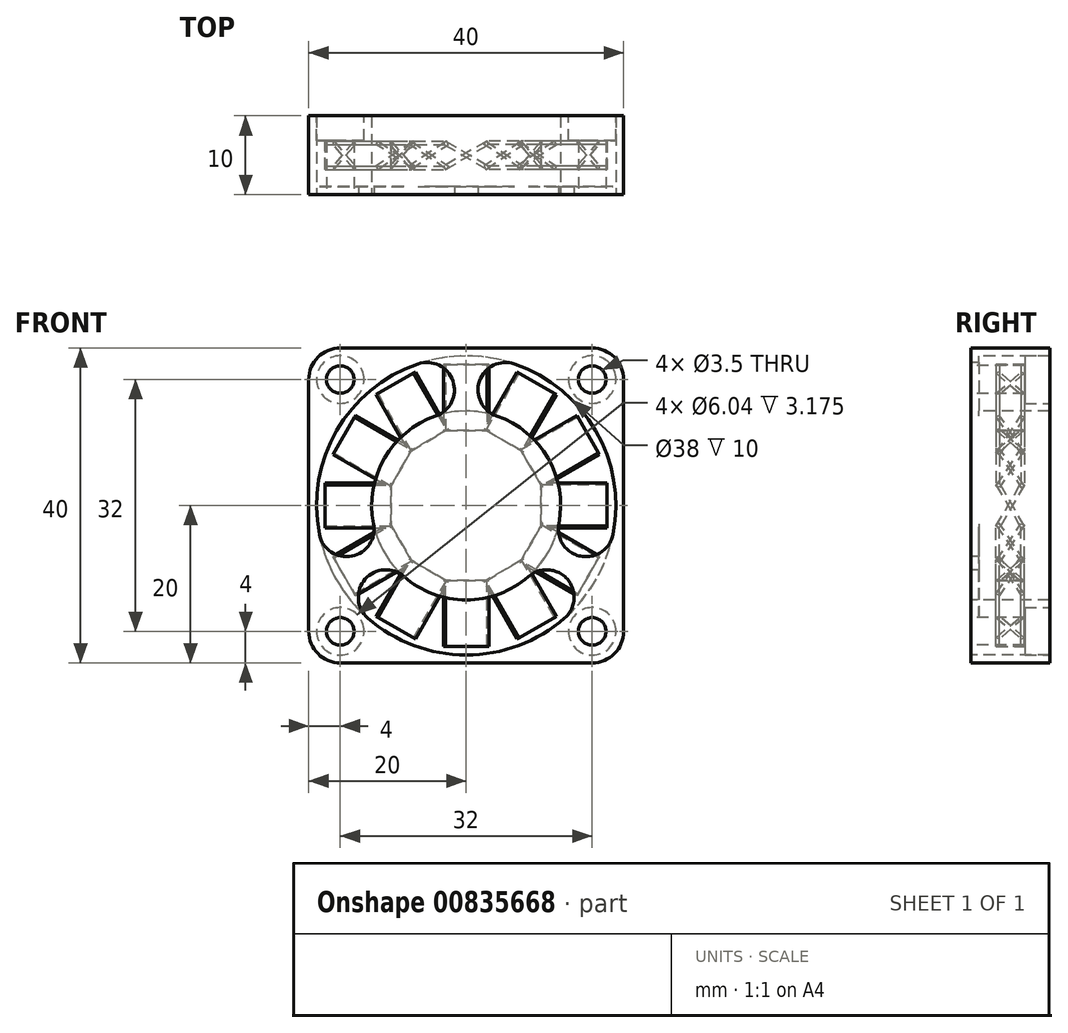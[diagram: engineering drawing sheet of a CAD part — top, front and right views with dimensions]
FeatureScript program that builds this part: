
annotation { "Feature Type Name" : "Feature", "Feature Type Description" : "" }
export const myFeature = defineFeature(function(context is Context, id is Id, definition is map)
    precondition{}
    {
        {
            var Q0;
            Q0=qCreatedBy(makeId("Front.planeOp"),FACE);
            var sketch = newSketch(context, id + "F0", { "sketchPlane" : qUnion([Q0])});
            skLineSegment(sketch, "E0.bottom", {"start": v(-20, 20) * mm, "end": v(20, 20) * mm});
            skLineSegment(sketch, "E0.top", {"start": v(-20, -20) * mm, "end": v(20, -20) * mm});
            skLineSegment(sketch, "E0.left", {"start": v(-20, 20) * mm, "end": v(-20, -20) * mm});
            skLineSegment(sketch, "E0.right", {"start": v(20, 20) * mm, "end": v(20, -20) * mm});
            skLineSegment(sketch, "E1", {"start": v(-20, -20) * mm, "end": v(20, 20) * mm, "construction": true});
            skSolve(sketch);
        }
        {
            var Q0;
            Q0=makeQuery(id+"F0.imprint","IMPRINT",FACE,{"disambiguationData":[TD([[makeQuery(id+"F0.imprint","IMPRINT",EDGE,{"derivedFrom":sQuery(id+"F0.wireOp",EDGE,"E0.bottom")}),-1.0]])]});
            extrude(context, id + "F1", {"entities" : qUnion([Q0]), "depth" : 10 * mm, "offsetDistance" : 25.4 * mm});
        }
        {
            var Q0;
            Q0=makeQuery(id+"F1.opExtrude","SWEPT_EDGE",EDGE,{"disambiguationData":[OSD([sQuery(id+"F0.wireOp",EDGE,"E0.top"),sQuery(id+"F0.wireOp",EDGE,"E0.left")])]});
            var Q1;
            Q1=makeQuery(id+"F1.opExtrude","SWEPT_EDGE",EDGE,{"disambiguationData":[OSD([sQuery(id+"F0.wireOp",EDGE,"E0.top"),sQuery(id+"F0.wireOp",EDGE,"E0.right")])]});
            var Q2;
            Q2=makeQuery(id+"F1.opExtrude","SWEPT_EDGE",EDGE,{"disambiguationData":[OSD([sQuery(id+"F0.wireOp",EDGE,"E0.bottom"),sQuery(id+"F0.wireOp",EDGE,"E0.right")])]});
            var Q3;
            Q3=makeQuery(id+"F1.opExtrude","SWEPT_EDGE",EDGE,{"disambiguationData":[OSD([sQuery(id+"F0.wireOp",EDGE,"E0.bottom"),sQuery(id+"F0.wireOp",EDGE,"E0.left")])]});
            fillet(context, id + "F2", {"entities" : qUnion([Q0, Q1, Q2, Q3]), "radius" : 4 * mm, "tangentPropagation" : true, "allowEdgeOverflow" : false});
        }
        {
            var Q0;
            Q0=makeQuery(id+"F1.opExtrude","CAP_FACE",FACE,{"disambiguationData":[OSD([sQuery(id+"F0.wireOp",EDGE,"E0.bottom"),sQuery(id+"F0.wireOp",EDGE,"E0.top"),sQuery(id+"F0.wireOp",EDGE,"E0.left"),sQuery(id+"F0.wireOp",EDGE,"E0.right")])],"isStart":true});
            shell(context, id + "F3", {"entities" : qUnion([Q0]), "thickness" : 1 * mm});
        }
        {
            var Q0;
            Q0=makeQuery(id+"F1.opExtrude","CAP_FACE",FACE,{"disambiguationData":[OSD([sQuery(id+"F0.wireOp",EDGE,"E0.bottom"),sQuery(id+"F0.wireOp",EDGE,"E0.top"),sQuery(id+"F0.wireOp",EDGE,"E0.left"),sQuery(id+"F0.wireOp",EDGE,"E0.right")])],"isStart":false});
            var sketch = newSketch(context, id + "F4", { "sketchPlane" : qUnion([Q0])});
            skArc(sketch, "E2", {"start": v(-1.5, 11.9) * mm, "mid": v(-10.4, 6) * mm, "end": v(-11.06, -4.65) * mm});
            skArc(sketch, "E3", {"start": v(-1.5, 18.94) * mm, "mid": v(-16.45, 9.5) * mm, "end": v(-17.15, -8.17) * mm});
            skLineSegment(sketch, "E4", {"start": v(-1.5, 18.94) * mm, "end": v(-1.5, 11.9) * mm});
            skLineSegment(sketch, "E5", {"start": v(1.5, 18.94) * mm, "end": v(1.5, 11.9) * mm});
            skLineSegment(sketch, "E6.1.0", {"start": v(-15.65, -10.77) * mm, "end": v(-9.56, -7.25) * mm});
            skLineSegment(sketch, "E6.1.1", {"start": v(-17.15, -8.17) * mm, "end": v(-11.06, -4.65) * mm});
            skLineSegment(sketch, "E6.2.0", {"start": v(17.15, -8.17) * mm, "end": v(11.06, -4.65) * mm});
            skLineSegment(sketch, "E6.2.1", {"start": v(15.65, -10.77) * mm, "end": v(9.56, -7.25) * mm});
            skArc(sketch, "E7.trimOffspring", {"start": v(-9.56, -7.25) * mm, "mid": v(0, -12) * mm, "end": v(9.56, -7.25) * mm});
            skArc(sketch, "E8.trimOffspring", {"start": v(-15.65, -10.77) * mm, "mid": v(0, -19) * mm, "end": v(15.65, -10.77) * mm});
            skArc(sketch, "E9.trimOffspring", {"start": v(11.06, -4.65) * mm, "mid": v(10.4, 6) * mm, "end": v(1.5, 11.9) * mm});
            skArc(sketch, "E10.trimOffspring", {"start": v(17.15, -8.17) * mm, "mid": v(16.45, 9.5) * mm, "end": v(1.5, 18.94) * mm});
            skSolve(sketch);
        }
        {
            var Q0;
            Q0 = qSketchRegion(id + "F4", true);
            extrude(context, id + "F5", {"entities" : qUnion([Q0]), "operationType" : NewBodyOperationType.REMOVE, "endBound" : BoundingType.THROUGH_ALL, "oppositeDirection" : true, "depth" : 25.4 * mm, "offsetDistance" : 25.4 * mm});
        }
        {
            var Q0;
            Q0=makeQuery(id+"F1.opExtrude","CAP_FACE",FACE,{"disambiguationData":[OSD([sQuery(id+"F0.wireOp",EDGE,"E0.bottom"),sQuery(id+"F0.wireOp",EDGE,"E0.top"),sQuery(id+"F0.wireOp",EDGE,"E0.left"),sQuery(id+"F0.wireOp",EDGE,"E0.right")])],"isStart":false});
            var sketch = newSketch(context, id + "F6", { "sketchPlane" : qUnion([Q0])});
            skArc(sketch, "E11", {"start": v(6.13, 17.98) * mm, "mid": v(1.69, 15.8) * mm, "end": v(3.87, 11.36) * mm});
            skArc(sketch, "E12", {"start": v(11.77, -2.33) * mm, "mid": v(14.53, -6.44) * mm, "end": v(18.64, -3.68) * mm});
            skLineSegment(sketch, "E13.0", {"start": v(1.5, 18.94) * mm, "end": v(1.5, 11.9) * mm});
            skLineSegment(sketch, "E14.0", {"start": v(17.15, -8.17) * mm, "end": v(11.06, -4.65) * mm});
            skArc(sketch, "E15", {"start": v(6.13, 17.98) * mm, "mid": v(3.84, 18.6) * mm, "end": v(1.5, 18.94) * mm});
            skArc(sketch, "E16", {"start": v(1.5, 11.9) * mm, "mid": v(2.67, 11.57) * mm, "end": v(3.87, 11.36) * mm});
            skArc(sketch, "E17", {"start": v(11.77, -2.33) * mm, "mid": v(11.36, -3.47) * mm, "end": v(11.06, -4.65) * mm});
            skArc(sketch, "E18", {"start": v(17.15, -8.17) * mm, "mid": v(18.04, -5.97) * mm, "end": v(18.64, -3.68) * mm});
            skArc(sketch, "E19.1.0", {"start": v(-1.5, 18.94) * mm, "mid": v(-3.84, 18.6) * mm, "end": v(-6.13, 17.98) * mm});
            skLineSegment(sketch, "E19.1.1", {"start": v(-17.15, -8.17) * mm, "end": v(-11.06, -4.65) * mm});
            skLineSegment(sketch, "E19.1.2", {"start": v(-1.5, 18.94) * mm, "end": v(-1.5, 11.9) * mm});
            skArc(sketch, "E19.1.3", {"start": v(-3.87, 11.36) * mm, "mid": v(-1.69, 15.8) * mm, "end": v(-6.13, 17.98) * mm});
            skArc(sketch, "E19.1.4", {"start": v(-18.64, -3.68) * mm, "mid": v(-14.53, -6.44) * mm, "end": v(-11.77, -2.33) * mm});
            skArc(sketch, "E19.1.5", {"start": v(-18.64, -3.68) * mm, "mid": v(-18.04, -5.97) * mm, "end": v(-17.15, -8.17) * mm});
            skArc(sketch, "E19.1.6", {"start": v(-3.87, 11.36) * mm, "mid": v(-2.67, 11.57) * mm, "end": v(-1.5, 11.9) * mm});
            skArc(sketch, "E19.1.7", {"start": v(-11.06, -4.65) * mm, "mid": v(-11.36, -3.47) * mm, "end": v(-11.77, -2.33) * mm});
            skArc(sketch, "E19.2.0", {"start": v(-15.65, -10.77) * mm, "mid": v(-14.2, -12.63) * mm, "end": v(-12.51, -14.3) * mm});
            skLineSegment(sketch, "E19.2.1", {"start": v(15.65, -10.77) * mm, "end": v(9.56, -7.25) * mm});
            skLineSegment(sketch, "E19.2.2", {"start": v(-15.65, -10.77) * mm, "end": v(-9.56, -7.25) * mm});
            skArc(sketch, "E19.2.3", {"start": v(-7.9, -9.03) * mm, "mid": v(-12.84, -9.36) * mm, "end": v(-12.51, -14.3) * mm});
            skArc(sketch, "E19.2.4", {"start": v(12.51, -14.3) * mm, "mid": v(12.84, -9.36) * mm, "end": v(7.9, -9.03) * mm});
            skArc(sketch, "E19.2.5", {"start": v(12.51, -14.3) * mm, "mid": v(14.2, -12.63) * mm, "end": v(15.65, -10.77) * mm});
            skArc(sketch, "E19.2.6", {"start": v(-7.9, -9.03) * mm, "mid": v(-8.69, -8.1) * mm, "end": v(-9.56, -7.25) * mm});
            skArc(sketch, "E19.2.7", {"start": v(9.56, -7.25) * mm, "mid": v(8.69, -8.1) * mm, "end": v(7.9, -9.03) * mm});
            skSolve(sketch);
        }
        {
            var Q0;
            Q0 = qSketchRegion(id + "F6", true);
            var Q1;
            Q1=makeQuery(id+"F3.opShell","OFFSET_FACE",FACE,{"disambiguationData":[OSD([sQuery(id+"F0.wireOp",EDGE,"E0.bottom"),sQuery(id+"F0.wireOp",EDGE,"E0.top"),sQuery(id+"F0.wireOp",EDGE,"E0.left"),sQuery(id+"F0.wireOp",EDGE,"E0.right")])]});
            extrude(context, id + "F7", {"entities" : qUnion([Q0]), "operationType" : NewBodyOperationType.ADD, "oppositeDirection" : true, "depth" : 1 * mm, "endBoundEntityFace" : qUnion([Q1]), "offsetDistance" : 25.4 * mm});
        }
        {
            var Q0;
            {var subQ0=sQuery(id+"F6.wireOp",EDGE,"E19.2.3");var subQ1=sQuery(id+"F6.wireOp",EDGE,"E19.2.2");var subQ2=sQuery(id+"F6.wireOp",EDGE,"E19.2.4");var subQ3=sQuery(id+"F6.wireOp",EDGE,"E19.2.1");var subQ4=sQuery(id+"F6.wireOp",EDGE,"E19.1.3");var subQ5=sQuery(id+"F6.wireOp",EDGE,"E19.1.2");var subQ6=sQuery(id+"F6.wireOp",EDGE,"E19.1.4");var subQ7=sQuery(id+"F6.wireOp",EDGE,"E19.1.1");var subQ8=sQuery(id+"F6.wireOp",EDGE,"E14.0");var subQ9=sQuery(id+"F6.wireOp",EDGE,"E12");var subQ10=sQuery(id+"F6.wireOp",EDGE,"E13.0");var subQ11=sQuery(id+"F6.wireOp",EDGE,"E11");Q0=makeQuery(id+"F7.boolean.opBoolean","MERGE",FACE,{"derivedFrom":[makeQuery(id+"F3.opShell","OFFSET_FACE",FACE,{"disambiguationData":[OSD([sQuery(id+"F0.wireOp",EDGE,"E0.bottom"),sQuery(id+"F0.wireOp",EDGE,"E0.top"),sQuery(id+"F0.wireOp",EDGE,"E0.left"),sQuery(id+"F0.wireOp",EDGE,"E0.right")])]}),makeQuery(id+"F7.opExtrude","CAP_FACE",FACE,{"disambiguationData":[OSD([subQ11,subQ10,sQuery(id+"F6.wireOp",EDGE,"E15")])],"isStart":false}),makeQuery(id+"F7.opExtrude","CAP_FACE",FACE,{"disambiguationData":[OSD([subQ11,subQ10,sQuery(id+"F6.wireOp",EDGE,"E16")])],"isStart":false}),makeQuery(id+"F7.opExtrude","CAP_FACE",FACE,{"disambiguationData":[OSD([subQ9,subQ8,sQuery(id+"F6.wireOp",EDGE,"E17")])],"isStart":false}),makeQuery(id+"F7.opExtrude","CAP_FACE",FACE,{"disambiguationData":[OSD([subQ9,subQ8,sQuery(id+"F6.wireOp",EDGE,"E18")])],"isStart":false}),makeQuery(id+"F7.opExtrude","CAP_FACE",FACE,{"disambiguationData":[OSD([sQuery(id+"F6.wireOp",EDGE,"E19.1.0"),subQ5,subQ4])],"isStart":false}),makeQuery(id+"F7.opExtrude","CAP_FACE",FACE,{"disambiguationData":[OSD([subQ7,subQ6,sQuery(id+"F6.wireOp",EDGE,"E19.1.5")])],"isStart":false}),makeQuery(id+"F7.opExtrude","CAP_FACE",FACE,{"disambiguationData":[OSD([subQ7,subQ6,sQuery(id+"F6.wireOp",EDGE,"E19.1.7")])],"isStart":false}),makeQuery(id+"F7.opExtrude","CAP_FACE",FACE,{"disambiguationData":[OSD([subQ5,subQ4,sQuery(id+"F6.wireOp",EDGE,"E19.1.6")])],"isStart":false}),makeQuery(id+"F7.opExtrude","CAP_FACE",FACE,{"disambiguationData":[OSD([sQuery(id+"F6.wireOp",EDGE,"E19.2.0"),subQ1,subQ0])],"isStart":false}),makeQuery(id+"F7.opExtrude","CAP_FACE",FACE,{"disambiguationData":[OSD([subQ3,subQ2,sQuery(id+"F6.wireOp",EDGE,"E19.2.5")])],"isStart":false}),makeQuery(id+"F7.opExtrude","CAP_FACE",FACE,{"disambiguationData":[OSD([subQ3,subQ2,sQuery(id+"F6.wireOp",EDGE,"E19.2.7")])],"isStart":false}),makeQuery(id+"F7.opExtrude","CAP_FACE",FACE,{"disambiguationData":[OSD([subQ1,subQ0,sQuery(id+"F6.wireOp",EDGE,"E19.2.6")])],"isStart":false})]});}
            var sketch = newSketch(context, id + "F8", { "sketchPlane" : qUnion([Q0])});
            skCircle(sketch, "E20", {"center": v(0, 0) * mm, "radius": 12 * mm});
            skSolve(sketch);
        }
        {
            var Q0;
            {var subQ0=sQuery(id+"F8.wireOp",EDGE,"E20");var subQ1=sQuery(id+"F6.wireOp",EDGE,"E19.1.3");var subQ3=makeQuery(id+"F6.imprint","INTERSECT",VERTEX,{"derivedFrom":[sQuery(id+"F6.wireOp",EDGE,"E19.1.2"),subQ1]});var subQ5=makeQuery(id+"F8.imprint","INTERSECT",VERTEX,{"derivedFrom":[makeQuery(id+"F7.boolean.opBoolean","MERGE",EDGE,{"derivedFrom":[makeQuery(id+"F7.opExtrude","CAP_EDGE",EDGE,{"disambiguationData":[OSD([subQ1]),TDD([makeQuery(id+"F6.imprint","IMPRINT",EDGE,{"disambiguationData":[TD([[subQ3,1.0]])],"derivedFrom":subQ1})])],"isStart":false}),makeQuery(id+"F7.opExtrude","CAP_EDGE",EDGE,{"disambiguationData":[OSD([subQ1]),TDD([makeQuery(id+"F6.imprint","IMPRINT",EDGE,{"disambiguationData":[TD([[subQ3,-1.0]])],"derivedFrom":subQ1})])],"isStart":false})]}),subQ0]});var subQ19=sQuery(id+"F6.wireOp",EDGE,"E11");var subQ20=makeQuery(id+"F6.imprint","INTERSECT",VERTEX,{"derivedFrom":[subQ19,sQuery(id+"F6.wireOp",EDGE,"E13.0")]});var subQ21=makeQuery(id+"F8.imprint","INTERSECT",VERTEX,{"derivedFrom":[makeQuery(id+"F7.boolean.opBoolean","MERGE",EDGE,{"derivedFrom":[makeQuery(id+"F7.opExtrude","CAP_EDGE",EDGE,{"disambiguationData":[OSD([subQ19]),TDD([makeQuery(id+"F6.imprint","IMPRINT",EDGE,{"disambiguationData":[TD([[subQ20,1.0]])],"derivedFrom":subQ19})])],"isStart":false}),makeQuery(id+"F7.opExtrude","CAP_EDGE",EDGE,{"disambiguationData":[OSD([subQ19]),TDD([makeQuery(id+"F6.imprint","IMPRINT",EDGE,{"disambiguationData":[TD([[subQ20,-1.0]])],"derivedFrom":subQ19})])],"isStart":false})]}),subQ0]});Q0=makeQuery(id+"F8.imprint","IMPRINT",FACE,{"disambiguationData":[TD([[makeQuery(id+"F8.imprint","IMPRINT",EDGE,{"disambiguationData":[TD([[subQ21,1.0],[subQ5,-1.0]])],"derivedFrom":subQ0}),1.0]])]});}
            var Q1;
            Q1=makeQuery(id+"F1.opExtrude","CAP_FACE",FACE,{"disambiguationData":[OSD([sQuery(id+"F0.wireOp",EDGE,"E0.bottom"),sQuery(id+"F0.wireOp",EDGE,"E0.top"),sQuery(id+"F0.wireOp",EDGE,"E0.left"),sQuery(id+"F0.wireOp",EDGE,"E0.right")])],"isStart":true});
            extrude(context, id + "F9", {"entities" : qUnion([Q0]), "operationType" : NewBodyOperationType.ADD, "endBound" : BoundingType.UP_TO_SURFACE, "depth" : 25.4 * mm, "endBoundEntityFace" : qUnion([Q1]), "offsetDistance" : 25.4 * mm});
        }
        {
            var Q0;
            Q0=qCreatedBy(makeId("Top.planeOp"),FACE);
            cPlane(context, id + "F10", {"entities" : qUnion([Q0]), "cplaneType" : CPlaneType.OFFSET, "offset" : 9.52 * mm, "width" : 152.4 * mm, "height" : 152.4 * mm});
        }
        {
            var Q0;
            Q0=qCreatedBy(id+"F10.planeOp",FACE);
            var sketch = newSketch(context, id + "F11", { "sketchPlane" : qUnion([Q0])});
            skLineSegment(sketch, "E21", {"start": v(-2.75, -3.41) * mm, "end": v(2.75, -6.59) * mm, "construction": true});
            skLineSegment(sketch, "E22", {"start": v(-16, -5) * mm, "end": v(0, -5) * mm, "construction": true});
            skLineSegment(sketch, "E23", {"start": v(-2.87, -3.63) * mm, "end": v(-2.62, -3.2) * mm});
            skLineSegment(sketch, "E24", {"start": v(-2.62, -3.2) * mm, "end": v(2.87, -6.37) * mm});
            skLineSegment(sketch, "E25", {"start": v(2.87, -6.37) * mm, "end": v(2.62, -6.8) * mm});
            skLineSegment(sketch, "E26", {"start": v(2.62, -6.8) * mm, "end": v(-2.87, -3.63) * mm});
            skSolve(sketch);
        }
        {
            var Q0;
            Q0 = qSketchRegion(id + "F11", true);
            extrude(context, id + "F12", {"entities" : qUnion([Q0]), "depth" : 8.38 * mm, "offsetDistance" : 25.4 * mm});
        }
        {
            var Q0;
            Q0=makeQuery(id+"F12.opExtrude","SWEPT_BODY",BODY,{"disambiguationData":[OSD([sQuery(id+"F11.wireOp",EDGE,"E23"),sQuery(id+"F11.wireOp",EDGE,"E24"),sQuery(id+"F11.wireOp",EDGE,"E25"),sQuery(id+"F11.wireOp",EDGE,"E26")])]});
            var Q1;
            Q1=makeQuery(id+"F9.boolean.opBoolean","MERGE",FACE,{"derivedFrom":[makeQuery(id+"F5.boolean.opBoolean","COPY",FACE,{"derivedFrom":makeQuery(id+"F5.opExtrude","SWEPT_FACE",FACE,{"disambiguationData":[OSD([sQuery(id+"F4.wireOp",EDGE,"E2")])]})}),makeQuery(id+"F5.boolean.opBoolean","COPY",FACE,{"derivedFrom":makeQuery(id+"F5.opExtrude","SWEPT_FACE",FACE,{"disambiguationData":[OSD([sQuery(id+"F4.wireOp",EDGE,"E7.trimOffspring")])]})}),makeQuery(id+"F5.boolean.opBoolean","COPY",FACE,{"derivedFrom":makeQuery(id+"F5.opExtrude","SWEPT_FACE",FACE,{"disambiguationData":[OSD([sQuery(id+"F4.wireOp",EDGE,"E9.trimOffspring")])]})}),makeQuery(id+"F9.opExtrude","SWEPT_FACE",FACE,{"disambiguationData":[OSD([sQuery(id+"F8.wireOp",EDGE,"E20")])]})]});
            circularPattern(context, id + "F13", {"entities" : qUnion([Q0]), "axis" : qUnion([Q1]), "angle" : 360 * degree, "instanceCount" : 12, "equalSpace" : true});
        }
        {
            var Q0;
            {var subQ0=sQuery(id+"F6.wireOp",EDGE,"E19.1.6");var subQ1=sQuery(id+"F6.wireOp",EDGE,"E19.1.3");var subQ2=sQuery(id+"F6.wireOp",EDGE,"E19.1.2");var subQ3=makeQuery(id+"F7.opExtrude","CAP_FACE",FACE,{"disambiguationData":[OSD([subQ2,subQ1,subQ0])],"isStart":false});var subQ4=sQuery(id+"F6.wireOp",EDGE,"E19.1.0");var subQ5=makeQuery(id+"F7.opExtrude","CAP_FACE",FACE,{"disambiguationData":[OSD([subQ4,subQ2,subQ1])],"isStart":false});var subQ6=sQuery(id+"F6.wireOp",EDGE,"E14.0");var subQ7=sQuery(id+"F6.wireOp",EDGE,"E12");var subQ8=makeQuery(id+"F7.opExtrude","CAP_FACE",FACE,{"disambiguationData":[OSD([subQ7,subQ6,sQuery(id+"F6.wireOp",EDGE,"E17")])],"isStart":false});var subQ9=sQuery(id+"F6.wireOp",EDGE,"E19.1.4");var subQ10=sQuery(id+"F6.wireOp",EDGE,"E19.1.1");var subQ11=makeQuery(id+"F7.opExtrude","CAP_FACE",FACE,{"disambiguationData":[OSD([subQ10,subQ9,sQuery(id+"F6.wireOp",EDGE,"E19.1.7")])],"isStart":false});var subQ12=sQuery(id+"F6.wireOp",EDGE,"E16");var subQ13=sQuery(id+"F6.wireOp",EDGE,"E13.0");var subQ14=sQuery(id+"F6.wireOp",EDGE,"E11");var subQ15=makeQuery(id+"F7.opExtrude","CAP_FACE",FACE,{"disambiguationData":[OSD([subQ14,subQ13,subQ12])],"isStart":false});var subQ16=sQuery(id+"F6.wireOp",EDGE,"E19.2.3");var subQ17=sQuery(id+"F6.wireOp",EDGE,"E19.2.2");var subQ18=makeQuery(id+"F7.opExtrude","CAP_FACE",FACE,{"disambiguationData":[OSD([subQ17,subQ16,sQuery(id+"F6.wireOp",EDGE,"E19.2.6")])],"isStart":false});var subQ21=makeQuery(id+"F7.opExtrude","CAP_FACE",FACE,{"disambiguationData":[OSD([subQ10,subQ9,sQuery(id+"F6.wireOp",EDGE,"E19.1.5")])],"isStart":false});var subQ22=sQuery(id+"F6.wireOp",EDGE,"E15");var subQ23=makeQuery(id+"F7.opExtrude","CAP_FACE",FACE,{"disambiguationData":[OSD([subQ14,subQ13,subQ22])],"isStart":false});var subQ27=sQuery(id+"F0.wireOp",EDGE,"E0.bottom");var subQ28=sQuery(id+"F0.wireOp",EDGE,"E0.right");var subQ29=makeQuery(id+"F7.opExtrude","CAP_FACE",FACE,{"disambiguationData":[OSD([subQ7,subQ6,sQuery(id+"F6.wireOp",EDGE,"E18")])],"isStart":false});var subQ30=sQuery(id+"F0.wireOp",EDGE,"E0.left");var subQ31=makeQuery(id+"F3.opShell","OFFSET_FACE",FACE,{"disambiguationData":[OSD([subQ27,sQuery(id+"F0.wireOp",EDGE,"E0.top"),subQ30,subQ28])]});var subQ33=makeQuery(id+"F7.opExtrude","CAP_FACE",FACE,{"disambiguationData":[OSD([sQuery(id+"F6.wireOp",EDGE,"E19.2.0"),subQ17,subQ16])],"isStart":false});var subQ34=sQuery(id+"F6.wireOp",EDGE,"E19.2.4");var subQ35=sQuery(id+"F6.wireOp",EDGE,"E19.2.1");var subQ36=makeQuery(id+"F7.opExtrude","CAP_FACE",FACE,{"disambiguationData":[OSD([subQ35,subQ34,sQuery(id+"F6.wireOp",EDGE,"E19.2.5")])],"isStart":false});var subQ37=makeQuery(id+"F7.opExtrude","CAP_FACE",FACE,{"disambiguationData":[OSD([subQ35,subQ34,sQuery(id+"F6.wireOp",EDGE,"E19.2.7")])],"isStart":false});Q0=makeQuery(id+"F9.boolean.opBoolean","SPLIT",FACE,{"disambiguationData":[TD([makeQuery(id+"F3.opShell","OFFSET_FACE",FACE,{"disambiguationData":[OSD([subQ27])]})])],"derivedFrom":makeQuery(id+"F7.boolean.opBoolean","MERGE",FACE,{"derivedFrom":[subQ31,subQ23,subQ15,subQ8,subQ29,subQ5,subQ21,subQ11,subQ3,subQ33,subQ36,subQ37,subQ18]})});}
            var sketch = newSketch(context, id + "F14", { "sketchPlane" : qUnion([Q0])});
            skLineSegment(sketch, "E27.0", {"start": v(16, 19) * mm, "end": v(-16, 19) * mm});
            skArc(sketch, "E27.1", {"start": v(-16, 19) * mm, "mid": v(-18.12, 18.12) * mm, "end": v(-19, 16) * mm});
            skLineSegment(sketch, "E27.2", {"start": v(-19, 16) * mm, "end": v(-19, -16) * mm});
            skLineSegment(sketch, "E27.3", {"start": v(19, 16) * mm, "end": v(19, -16) * mm});
            skArc(sketch, "E27.4", {"start": v(19, 16) * mm, "mid": v(18.12, 18.12) * mm, "end": v(16, 19) * mm});
            skArc(sketch, "E27.5", {"start": v(-19, -16) * mm, "mid": v(-18.12, -18.12) * mm, "end": v(-16, -19) * mm});
            skLineSegment(sketch, "E27.6", {"start": v(16, -19) * mm, "end": v(-16, -19) * mm});
            skArc(sketch, "E27.7", {"start": v(16, -19) * mm, "mid": v(18.12, -18.12) * mm, "end": v(19, -16) * mm});
            skCircle(sketch, "E28", {"center": v(0, 0) * mm, "radius": 19 * mm});
            skSolve(sketch);
        }
        {
            var Q0;
            {var subQ6=sQuery(id+"F14.wireOp",EDGE,"E27.1");Q0=makeQuery(id+"F14.imprint","IMPRINT",FACE,{"disambiguationData":[TD([[makeQuery(id+"F14.imprint","IMPRINT",EDGE,{"derivedFrom":subQ6}),-1.0]])]});}
            var Q1;
            {var subQ6=sQuery(id+"F14.wireOp",EDGE,"E27.4");Q1=makeQuery(id+"F14.imprint","IMPRINT",FACE,{"disambiguationData":[TD([[makeQuery(id+"F14.imprint","IMPRINT",EDGE,{"derivedFrom":subQ6}),-1.0]])]});}
            var Q2;
            {var subQ3=sQuery(id+"F14.wireOp",EDGE,"E27.7");Q2=makeQuery(id+"F14.imprint","IMPRINT",FACE,{"disambiguationData":[TD([[makeQuery(id+"F14.imprint","IMPRINT",EDGE,{"derivedFrom":subQ3}),1.0]])]});}
            var Q3;
            {var subQ3=sQuery(id+"F14.wireOp",EDGE,"E27.5");Q3=makeQuery(id+"F14.imprint","IMPRINT",FACE,{"disambiguationData":[TD([[makeQuery(id+"F14.imprint","IMPRINT",EDGE,{"derivedFrom":subQ3}),1.0]])]});}
            var Q4;
            Q4=makeQuery(id+"F1.opExtrude","CAP_FACE",FACE,{"disambiguationData":[OSD([sQuery(id+"F0.wireOp",EDGE,"E0.bottom"),sQuery(id+"F0.wireOp",EDGE,"E0.top"),sQuery(id+"F0.wireOp",EDGE,"E0.left"),sQuery(id+"F0.wireOp",EDGE,"E0.right")])],"isStart":true});
            extrude(context, id + "F15", {"entities" : qUnion([Q0, Q1, Q2, Q3]), "operationType" : NewBodyOperationType.ADD, "endBound" : BoundingType.UP_TO_SURFACE, "depth" : 25.4 * mm, "endBoundEntityFace" : qUnion([Q4]), "offsetDistance" : 25.4 * mm});
        }
        {
            var Q0;
            {var subQ0=sQuery(id+"F6.wireOp",EDGE,"E19.2.3");var subQ1=sQuery(id+"F6.wireOp",EDGE,"E19.2.2");var subQ2=sQuery(id+"F6.wireOp",EDGE,"E19.2.4");var subQ3=sQuery(id+"F6.wireOp",EDGE,"E19.2.1");var subQ4=sQuery(id+"F6.wireOp",EDGE,"E19.1.3");var subQ5=sQuery(id+"F6.wireOp",EDGE,"E19.1.2");var subQ6=sQuery(id+"F6.wireOp",EDGE,"E19.1.4");var subQ7=sQuery(id+"F6.wireOp",EDGE,"E19.1.1");var subQ8=sQuery(id+"F6.wireOp",EDGE,"E14.0");var subQ9=sQuery(id+"F6.wireOp",EDGE,"E12");var subQ10=sQuery(id+"F6.wireOp",EDGE,"E13.0");var subQ11=sQuery(id+"F6.wireOp",EDGE,"E11");Q0=makeQuery(id+"F7.boolean.opBoolean","MERGE",FACE,{"derivedFrom":[makeQuery(id+"F1.opExtrude","CAP_FACE",FACE,{"disambiguationData":[OSD([sQuery(id+"F0.wireOp",EDGE,"E0.bottom"),sQuery(id+"F0.wireOp",EDGE,"E0.top"),sQuery(id+"F0.wireOp",EDGE,"E0.left"),sQuery(id+"F0.wireOp",EDGE,"E0.right")])],"isStart":false}),makeQuery(id+"F7.opExtrude","CAP_FACE",FACE,{"disambiguationData":[OSD([subQ11,subQ10,sQuery(id+"F6.wireOp",EDGE,"E15")])],"isStart":true}),makeQuery(id+"F7.opExtrude","CAP_FACE",FACE,{"disambiguationData":[OSD([subQ11,subQ10,sQuery(id+"F6.wireOp",EDGE,"E16")])],"isStart":true}),makeQuery(id+"F7.opExtrude","CAP_FACE",FACE,{"disambiguationData":[OSD([subQ9,subQ8,sQuery(id+"F6.wireOp",EDGE,"E17")])],"isStart":true}),makeQuery(id+"F7.opExtrude","CAP_FACE",FACE,{"disambiguationData":[OSD([subQ9,subQ8,sQuery(id+"F6.wireOp",EDGE,"E18")])],"isStart":true}),makeQuery(id+"F7.opExtrude","CAP_FACE",FACE,{"disambiguationData":[OSD([sQuery(id+"F6.wireOp",EDGE,"E19.1.0"),subQ5,subQ4])],"isStart":true}),makeQuery(id+"F7.opExtrude","CAP_FACE",FACE,{"disambiguationData":[OSD([subQ7,subQ6,sQuery(id+"F6.wireOp",EDGE,"E19.1.5")])],"isStart":true}),makeQuery(id+"F7.opExtrude","CAP_FACE",FACE,{"disambiguationData":[OSD([subQ7,subQ6,sQuery(id+"F6.wireOp",EDGE,"E19.1.7")])],"isStart":true}),makeQuery(id+"F7.opExtrude","CAP_FACE",FACE,{"disambiguationData":[OSD([subQ5,subQ4,sQuery(id+"F6.wireOp",EDGE,"E19.1.6")])],"isStart":true}),makeQuery(id+"F7.opExtrude","CAP_FACE",FACE,{"disambiguationData":[OSD([sQuery(id+"F6.wireOp",EDGE,"E19.2.0"),subQ1,subQ0])],"isStart":true}),makeQuery(id+"F7.opExtrude","CAP_FACE",FACE,{"disambiguationData":[OSD([subQ3,subQ2,sQuery(id+"F6.wireOp",EDGE,"E19.2.5")])],"isStart":true}),makeQuery(id+"F7.opExtrude","CAP_FACE",FACE,{"disambiguationData":[OSD([subQ3,subQ2,sQuery(id+"F6.wireOp",EDGE,"E19.2.7")])],"isStart":true}),makeQuery(id+"F7.opExtrude","CAP_FACE",FACE,{"disambiguationData":[OSD([subQ1,subQ0,sQuery(id+"F6.wireOp",EDGE,"E19.2.6")])],"isStart":true})]});}
            var sketch = newSketch(context, id + "F16", { "sketchPlane" : qUnion([Q0])});
            skLineSegment(sketch, "E29.bottom", {"start": v(-16, 16) * mm, "end": v(16, 16) * mm, "construction": true});
            skLineSegment(sketch, "E29.top", {"start": v(-16, -16) * mm, "end": v(16, -16) * mm, "construction": true});
            skLineSegment(sketch, "E29.left", {"start": v(-16, 16) * mm, "end": v(-16, -16) * mm, "construction": true});
            skLineSegment(sketch, "E29.right", {"start": v(16, 16) * mm, "end": v(16, -16) * mm, "construction": true});
            skLineSegment(sketch, "E30", {"start": v(-16, -16) * mm, "end": v(16, 16) * mm, "construction": true});
            skSolve(sketch);
        }
        {
            var Q0;
            Q0=sQuery(id+"F16.wireOp",VERTEX,"E29.bottom.start");
            var Q1;
            Q1=sQuery(id+"F16.wireOp",VERTEX,"E29.bottom.end");
            var Q2;
            Q2=sQuery(id+"F16.wireOp",VERTEX,"E29.top.start");
            var Q3;
            Q3=sQuery(id+"F16.wireOp",VERTEX,"E29.top.end");
            var Q4;
            Q4=makeQuery(id+"F1.opExtrude","SWEPT_BODY",BODY,{"disambiguationData":[OSD([sQuery(id+"F0.wireOp",EDGE,"E0.bottom"),sQuery(id+"F0.wireOp",EDGE,"E0.top"),sQuery(id+"F0.wireOp",EDGE,"E0.left"),sQuery(id+"F0.wireOp",EDGE,"E0.right")])]});
            hole(context, id + "F17", {"style" : HoleStyle.SIMPLE, "endStyle" : HoleEndStyle.THROUGH, "holeDiameter" : 3.5 * mm, "majorDiameter" : 6.35 * mm, "isTappedThrough" : true, "tappedDepth" : 12.7 * mm, "tapClearance" : 3, "startFromSketch" : true, "locations" : qUnion([Q0, Q1, Q2, Q3]), "scope" : qUnion([Q4])});
        }
        {
            var Q0;
            {var subQ0=sQuery(id+"F14.wireOp",EDGE,"E28");var subQ1=sQuery(id+"F14.wireOp",EDGE,"E27.6");var subQ2=sQuery(id+"F14.wireOp",EDGE,"E27.3");var subQ3=sQuery(id+"F14.wireOp",EDGE,"E27.2");var subQ4=sQuery(id+"F14.wireOp",EDGE,"E27.0");Q0=makeQuery(id+"F15.boolean.opBoolean","MERGE",FACE,{"derivedFrom":[makeQuery(id+"F1.opExtrude","CAP_FACE",FACE,{"disambiguationData":[OSD([sQuery(id+"F0.wireOp",EDGE,"E0.bottom"),sQuery(id+"F0.wireOp",EDGE,"E0.top"),sQuery(id+"F0.wireOp",EDGE,"E0.left"),sQuery(id+"F0.wireOp",EDGE,"E0.right")])],"isStart":true}),makeQuery(id+"F15.opExtrude","CAP_FACE",FACE,{"disambiguationData":[OSD([subQ4,subQ2,sQuery(id+"F14.wireOp",EDGE,"E27.4"),subQ0])],"isStart":false}),makeQuery(id+"F15.opExtrude","CAP_FACE",FACE,{"disambiguationData":[OSD([subQ4,sQuery(id+"F14.wireOp",EDGE,"E27.1"),subQ3,subQ0])],"isStart":false}),makeQuery(id+"F15.opExtrude","CAP_FACE",FACE,{"disambiguationData":[OSD([subQ3,sQuery(id+"F14.wireOp",EDGE,"E27.5"),subQ1,subQ0])],"isStart":false}),makeQuery(id+"F15.opExtrude","CAP_FACE",FACE,{"disambiguationData":[OSD([subQ2,subQ1,sQuery(id+"F14.wireOp",EDGE,"E27.7"),subQ0])],"isStart":false})]});}
            var sketch = newSketch(context, id + "F18", { "sketchPlane" : qUnion([Q0])});
            skCircle(sketch, "E31.0", {"center": v(-16, 16) * mm, "radius": 1.75 * mm, "construction": true});
            skCircle(sketch, "E31.1", {"center": v(16, 16) * mm, "radius": 1.75 * mm, "construction": true});
            skCircle(sketch, "E31.2", {"center": v(16, -16) * mm, "radius": 1.75 * mm, "construction": true});
            skCircle(sketch, "E31.3", {"center": v(-16, -16) * mm, "radius": 1.75 * mm, "construction": true});
            skCircle(sketch, "E32.0", {"center": v(-16, 16) * mm, "radius": 3.02 * mm});
            skCircle(sketch, "E33.0", {"center": v(16, 16) * mm, "radius": 3.02 * mm});
            skCircle(sketch, "E34.0", {"center": v(-16, -16) * mm, "radius": 3.02 * mm});
            skCircle(sketch, "E35.0", {"center": v(16, -16) * mm, "radius": 3.02 * mm});
            skSolve(sketch);
        }
        {
            var Q0;
            Q0 = qSketchRegion(id + "F18", true);
            extrude(context, id + "F19", {"entities" : qUnion([Q0]), "operationType" : NewBodyOperationType.REMOVE, "oppositeDirection" : true, "depth" : 3.17 * mm, "offsetDistance" : 25.4 * mm});
        }
    });
